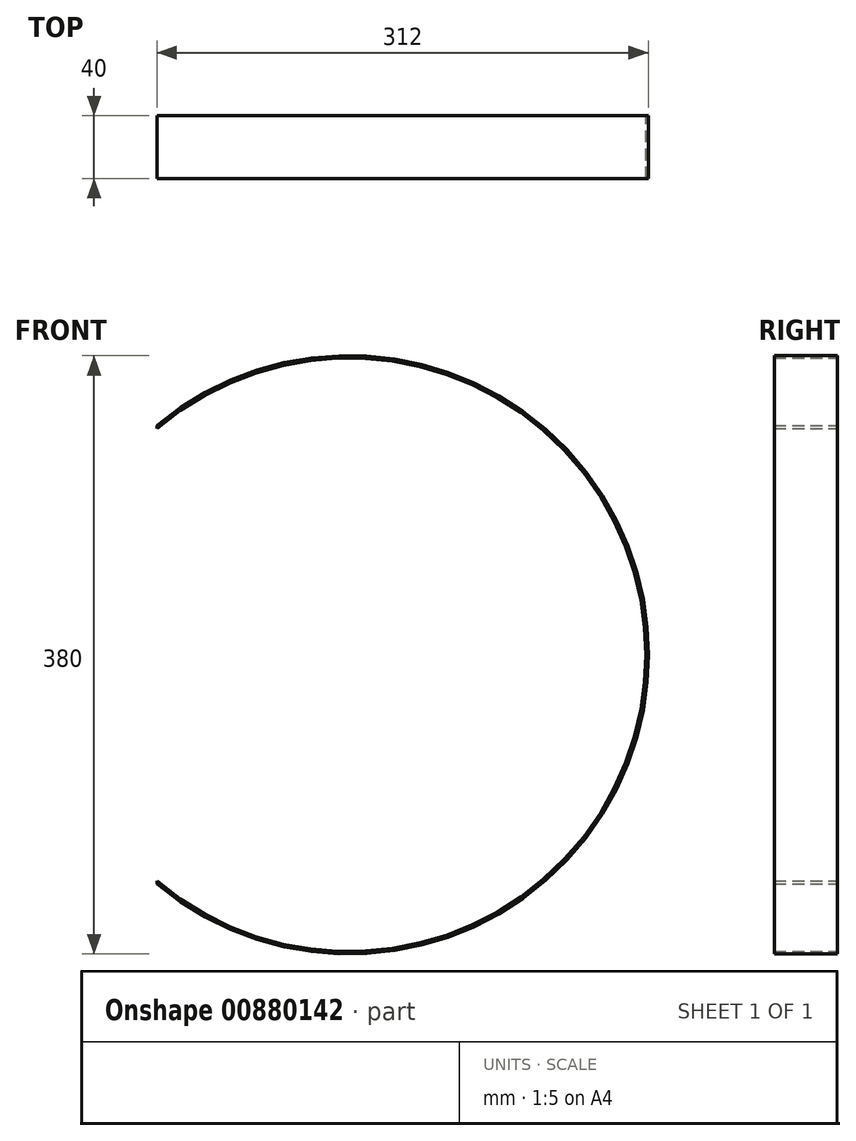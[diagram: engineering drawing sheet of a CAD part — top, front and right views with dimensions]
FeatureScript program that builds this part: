
annotation { "Feature Type Name" : "Feature", "Feature Type Description" : "" }
export const myFeature = defineFeature(function(context is Context, id is Id, definition is map)
    precondition{}
    {
        {
            var Q0;
            Q0=qCreatedBy(makeId("Front.planeOp"),FACE);
            var sketch = newSketch(context, id + "F0", { "sketchPlane" : qUnion([Q0])});
            skCircle(sketch, "E0", {"center": v(0, 0) * mm, "radius": 190 * mm});
            skLineSegment(sketch, "E1", {"start": v(0, 0) * mm, "end": v(-122, 0) * mm});
            skLineSegment(sketch, "E2", {"start": v(-122, 0) * mm, "end": v(-122, 145.66) * mm});
            skLineSegment(sketch, "E3", {"start": v(-122, 145.66) * mm, "end": v(-122, -145.66) * mm});
            skCircle(sketch, "E4", {"center": v(0, 0) * mm, "radius": 188.5 * mm});
            skSolve(sketch);
        }
        {
            var Q0;
            {var subQ0=sQuery(id+"F0.wireOp",EDGE,"E2");var subQ1=sQuery(id+"F0.wireOp",EDGE,"E0");var subQ2=makeQuery(id+"F0.imprint","INTERSECT",VERTEX,{"derivedFrom":[subQ1,subQ0]});Q0=makeQuery(id+"F0.imprint","IMPRINT",FACE,{"disambiguationData":[TD([[makeQuery(id+"F0.imprint","IMPRINT",EDGE,{"disambiguationData":[TD([[subQ2,1.0]])],"derivedFrom":subQ1}),1.0]])]});}
            extrude(context, id + "F1", {"entities" : qUnion([Q0]), "depth" : 40 * mm, "offsetDistance" : 25 * mm});
        }
    });
